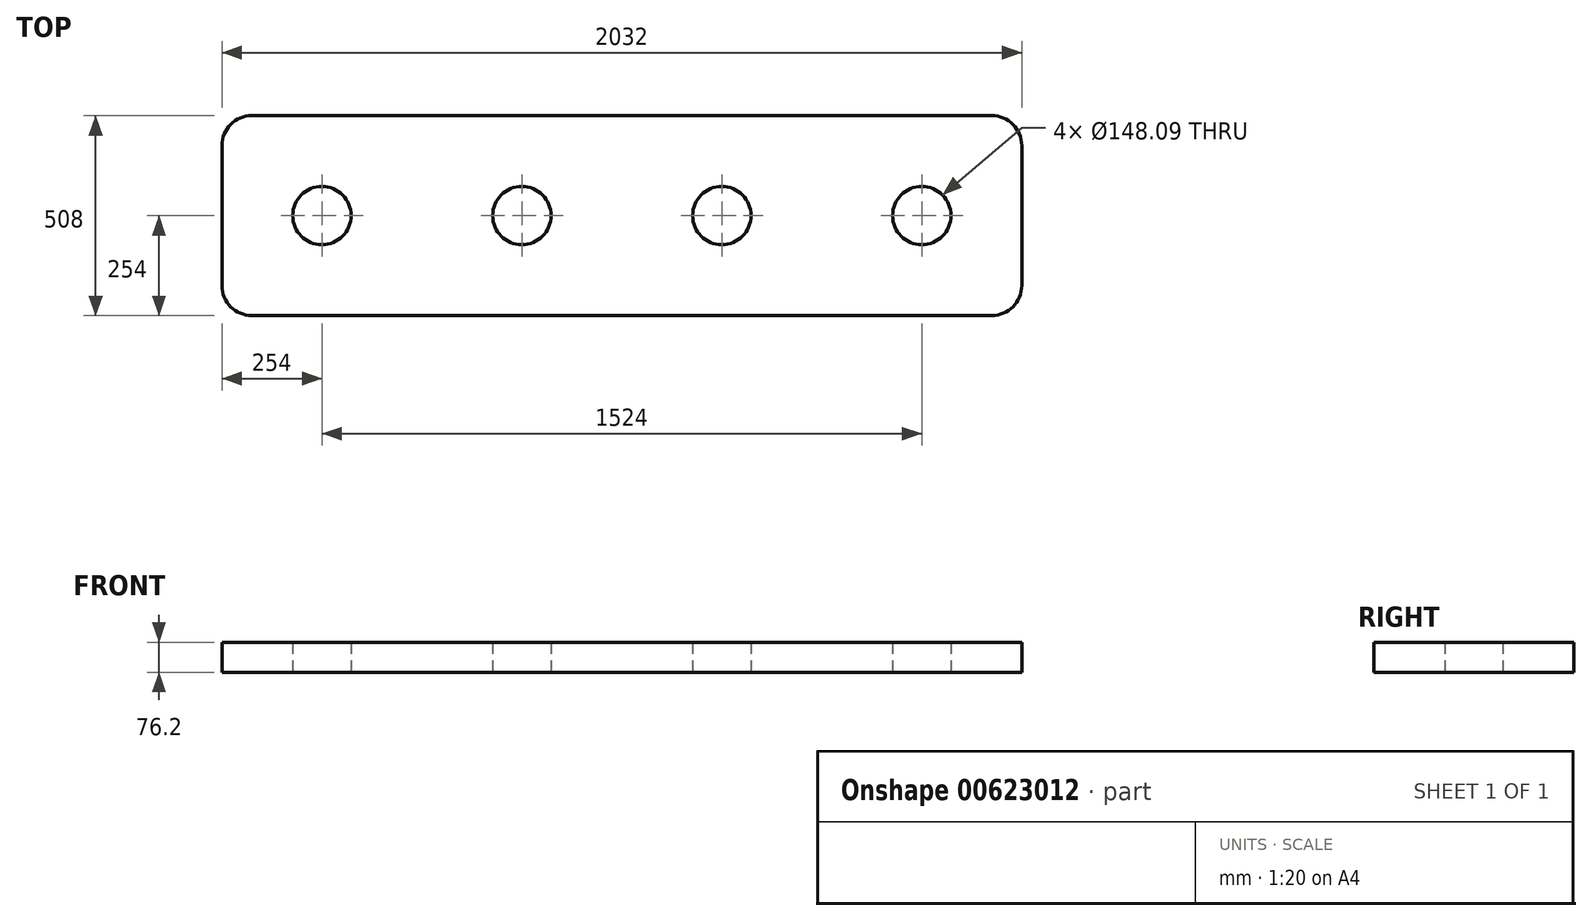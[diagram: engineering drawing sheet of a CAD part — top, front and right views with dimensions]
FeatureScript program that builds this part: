
annotation { "Feature Type Name" : "Feature", "Feature Type Description" : "" }
export const myFeature = defineFeature(function(context is Context, id is Id, definition is map)
    precondition{}
    {
        {
            var Q0;
            Q0=qCreatedBy(makeId("Top.planeOp"),FACE);
            var sketch = newSketch(context, id + "F0", { "sketchPlane" : qUnion([Q0])});
            skLineSegment(sketch, "E0.bottom", {"start": v(939.8, 254) * mm, "end": v(-939.8, 254) * mm});
            skLineSegment(sketch, "E0.top", {"start": v(939.8, -254) * mm, "end": v(-939.8, -254) * mm});
            skLineSegment(sketch, "E0.left", {"start": v(1016, 177.8) * mm, "end": v(1016, -177.8) * mm});
            skLineSegment(sketch, "E0.right", {"start": v(-1016, 177.8) * mm, "end": v(-1016, -177.8) * mm});
            skPoint(sketch, "E0.middle", {"position": v(0, 0) * mm});
            skCircle(sketch, "E1", {"center": v(-762, 0) * mm, "radius": 74.05 * mm});
            skCircle(sketch, "E2.1.0.0", {"center": v(-254, 0) * mm, "radius": 74.05 * mm});
            skCircle(sketch, "E2.2.0.0", {"center": v(254, 0) * mm, "radius": 74.05 * mm});
            skLineSegment(sketch, "E2.direction1", {"start": v(-762, 0) * mm, "end": v(-254, 0) * mm, "construction": true});
            skCircle(sketch, "E3.0.3.0", {"center": v(762, 0) * mm, "radius": 74.05 * mm});
            skPoint(sketch, "E4.visualSharp", {"position": v(1016, 254) * mm});
            skArc(sketch, "E4.filletArc", {"start": v(1016, 177.8) * mm, "mid": v(993.68, 231.68) * mm, "end": v(939.8, 254) * mm});
            skPoint(sketch, "E5.visualSharp", {"position": v(1016, -254) * mm});
            skArc(sketch, "E5.filletArc", {"start": v(939.8, -254) * mm, "mid": v(993.68, -231.68) * mm, "end": v(1016, -177.8) * mm});
            skPoint(sketch, "E6.visualSharp", {"position": v(-1016, -254) * mm});
            skArc(sketch, "E6.filletArc", {"start": v(-1016, -177.8) * mm, "mid": v(-993.68, -231.68) * mm, "end": v(-939.8, -254) * mm});
            skPoint(sketch, "E7.visualSharp", {"position": v(-1016, 254) * mm});
            skArc(sketch, "E7.filletArc", {"start": v(-939.8, 254) * mm, "mid": v(-993.68, 231.68) * mm, "end": v(-1016, 177.8) * mm});
            skSolve(sketch);
        }
        {
            var Q0;
            Q0 = qSketchRegion(id + "F0", true);
            extrude(context, id + "F1", {"entities" : qUnion([Q0]), "depth" : 76.2 * mm, "offsetDistance" : 25.4 * mm});
        }
    });
